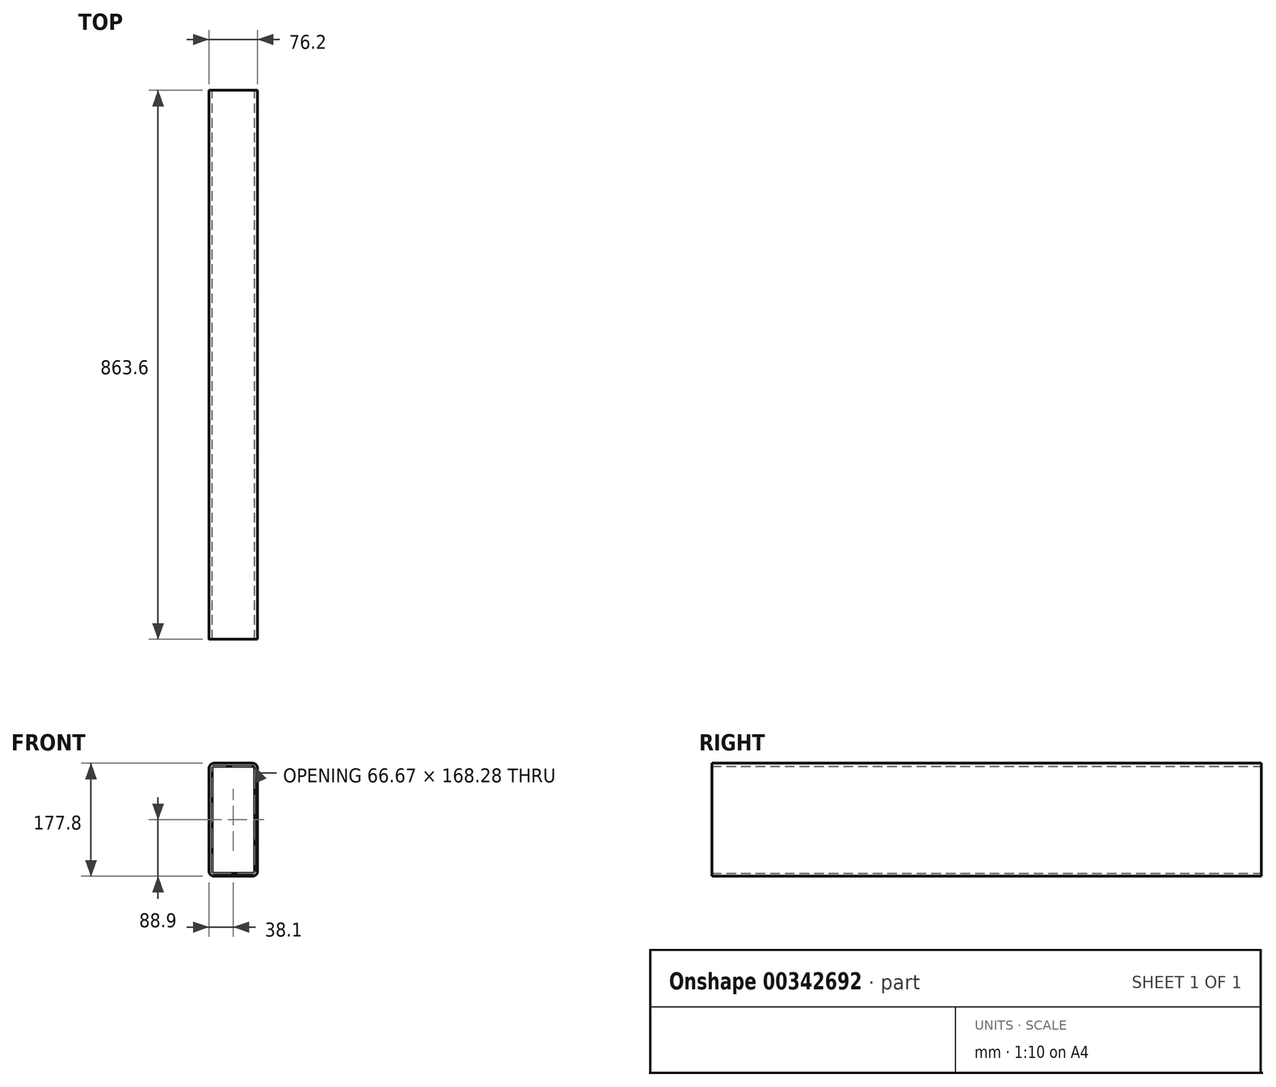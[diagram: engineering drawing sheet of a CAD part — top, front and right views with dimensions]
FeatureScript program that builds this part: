
annotation { "Feature Type Name" : "Feature", "Feature Type Description" : "" }
export const myFeature = defineFeature(function(context is Context, id is Id, definition is map)
    precondition{}
    {
        {
            var Q0;
            Q0=qCreatedBy(makeId("Front.planeOp"),FACE);
            var sketch = newSketch(context, id + "F0", { "sketchPlane" : qUnion([Q0])});
            skLineSegment(sketch, "E0.bottom", {"start": v(30.16, 88.9) * mm, "end": v(-30.16, 88.9) * mm});
            skLineSegment(sketch, "E0.top", {"start": v(30.16, -88.9) * mm, "end": v(-30.16, -88.9) * mm});
            skLineSegment(sketch, "E0.left", {"start": v(38.1, 80.96) * mm, "end": v(38.1, -80.96) * mm});
            skLineSegment(sketch, "E0.right", {"start": v(-38.1, 80.96) * mm, "end": v(-38.1, -80.96) * mm});
            skPoint(sketch, "E0.middle", {"position": v(0, 0) * mm});
            skPoint(sketch, "E1.visualSharp", {"position": v(-38.1, 88.9) * mm});
            skArc(sketch, "E1.filletArc", {"start": v(-30.16, 88.9) * mm, "mid": v(-35.78, 86.58) * mm, "end": v(-38.1, 80.96) * mm});
            skPoint(sketch, "E2.visualSharp", {"position": v(38.1, 88.9) * mm});
            skArc(sketch, "E2.filletArc", {"start": v(38.1, 80.96) * mm, "mid": v(35.78, 86.58) * mm, "end": v(30.16, 88.9) * mm});
            skPoint(sketch, "E3.visualSharp", {"position": v(38.1, -88.9) * mm});
            skArc(sketch, "E3.filletArc", {"start": v(30.16, -88.9) * mm, "mid": v(35.78, -86.58) * mm, "end": v(38.1, -80.96) * mm});
            skPoint(sketch, "E4.visualSharp", {"position": v(-38.1, -88.9) * mm});
            skArc(sketch, "E4.filletArc", {"start": v(-38.1, -80.96) * mm, "mid": v(-35.78, -86.58) * mm, "end": v(-30.16, -88.9) * mm});
            skArc(sketch, "E5.0", {"start": v(-30.16, 84.14) * mm, "mid": v(-32.4, 83.2) * mm, "end": v(-33.34, 80.96) * mm});
            skLineSegment(sketch, "E5.1", {"start": v(30.16, 84.14) * mm, "end": v(-30.16, 84.14) * mm});
            skLineSegment(sketch, "E5.2", {"start": v(-33.34, 80.96) * mm, "end": v(-33.34, -80.96) * mm});
            skArc(sketch, "E5.3", {"start": v(33.34, 80.96) * mm, "mid": v(32.4, 83.2) * mm, "end": v(30.16, 84.14) * mm});
            skArc(sketch, "E5.4", {"start": v(-33.34, -80.96) * mm, "mid": v(-32.4, -83.2) * mm, "end": v(-30.16, -84.14) * mm});
            skLineSegment(sketch, "E5.5", {"start": v(30.16, -84.14) * mm, "end": v(-30.16, -84.14) * mm});
            skArc(sketch, "E5.6", {"start": v(30.16, -84.14) * mm, "mid": v(32.4, -83.2) * mm, "end": v(33.34, -80.96) * mm});
            skLineSegment(sketch, "E5.7", {"start": v(33.34, 80.96) * mm, "end": v(33.34, -80.96) * mm});
            skSolve(sketch);
        }
        {
            var Q0;
            Q0=makeQuery(id+"F0.imprint","IMPRINT",FACE,{"disambiguationData":[TD([[makeQuery(id+"F0.imprint","IMPRINT",EDGE,{"derivedFrom":sQuery(id+"F0.wireOp",EDGE,"E0.bottom")}),1.0]])]});
            extrude(context, id + "F1", {"entities" : qUnion([Q0]), "depth" : 863.6 * mm});
        }
    });
